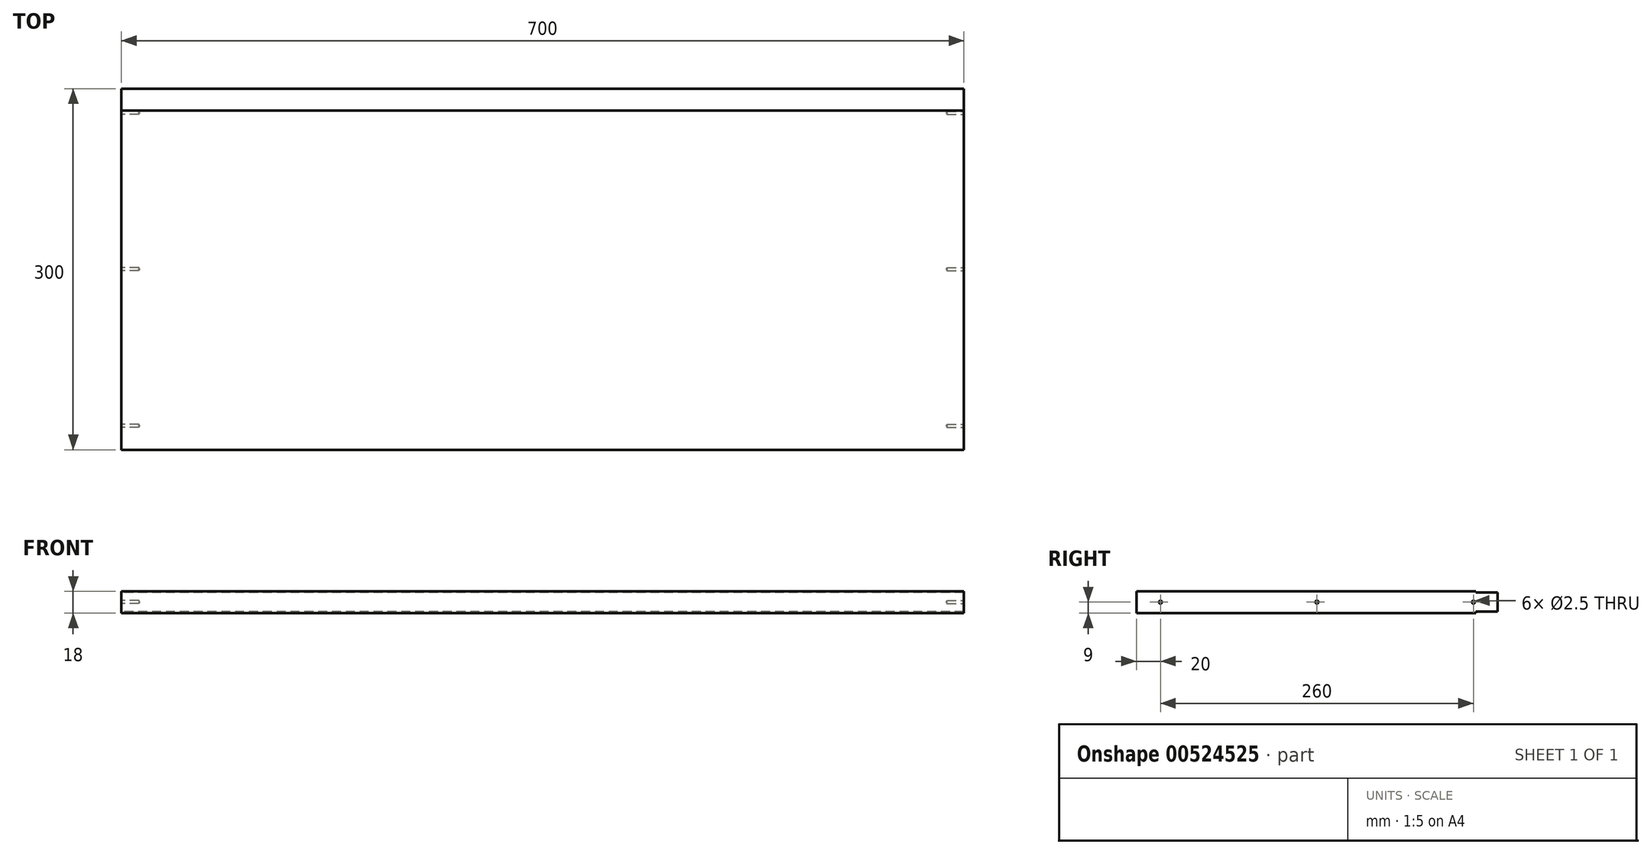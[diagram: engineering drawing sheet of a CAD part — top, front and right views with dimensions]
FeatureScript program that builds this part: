
annotation { "Feature Type Name" : "Feature", "Feature Type Description" : "" }
export const myFeature = defineFeature(function(context is Context, id is Id, definition is map)
    precondition{}
    {
        {
            var Q0;
            Q0=qCreatedBy(makeId("Top.planeOp"),FACE);
            var sketch = newSketch(context, id + "F0", { "sketchPlane" : qUnion([Q0])});
            skLineSegment(sketch, "E0.bottom", {"start": v(0, 0) * mm, "end": v(700, 0) * mm});
            skLineSegment(sketch, "E0.top", {"start": v(0, 300) * mm, "end": v(700, 300) * mm});
            skLineSegment(sketch, "E0.left", {"start": v(0, 0) * mm, "end": v(0, 300) * mm});
            skLineSegment(sketch, "E0.right", {"start": v(700, 0) * mm, "end": v(700, 300) * mm});
            skSolve(sketch);
        }
        {
            var Q0;
            Q0 = qSketchRegion(id + "F0", true);
            extrude(context, id + "F1", {"entities" : qUnion([Q0]), "depth" : 18 * mm, "offsetDistance" : 25 * mm});
        }
        {
            var Q0;
            Q0=makeQuery(id+"F1.opExtrude","SWEPT_FACE",FACE,{"disambiguationData":[OSD([sQuery(id+"F0.wireOp",EDGE,"E0.left")])]});
            var sketch = newSketch(context, id + "F2", { "sketchPlane" : qUnion([Q0])});
            skLineSegment(sketch, "E1.bottom", {"start": v(-300, 18) * mm, "end": v(-282, 18) * mm});
            skLineSegment(sketch, "E1.top", {"start": v(-300, 17) * mm, "end": v(-282, 17) * mm});
            skLineSegment(sketch, "E1.left", {"start": v(-300, 18) * mm, "end": v(-300, 17) * mm});
            skLineSegment(sketch, "E1.right", {"start": v(-282, 18) * mm, "end": v(-282, 17) * mm});
            skLineSegment(sketch, "E2.bottom", {"start": v(-300, 0) * mm, "end": v(-282, 0) * mm});
            skLineSegment(sketch, "E2.top", {"start": v(-300, 1) * mm, "end": v(-282, 1) * mm});
            skLineSegment(sketch, "E2.left", {"start": v(-300, 0) * mm, "end": v(-300, 1) * mm});
            skLineSegment(sketch, "E2.right", {"start": v(-282, 0) * mm, "end": v(-282, 1) * mm});
            skSolve(sketch);
        }
        {
            var Q0;
            Q0 = qSketchRegion(id + "F2", true);
            extrude(context, id + "F3", {"entities" : qUnion([Q0]), "operationType" : NewBodyOperationType.REMOVE, "endBound" : BoundingType.THROUGH_ALL, "oppositeDirection" : true, "depth" : 25 * mm, "offsetDistance" : 25 * mm});
        }
        {
            var Q0;
            Q0=makeQuery(id+"F1.opExtrude","SWEPT_FACE",FACE,{"disambiguationData":[OSD([sQuery(id+"F0.wireOp",EDGE,"E0.left")])]});
            var sketch = newSketch(context, id + "F4", { "sketchPlane" : qUnion([Q0])});
            skPoint(sketch, "E3", {"position": v(-280, 9) * mm});
            skPoint(sketch, "E4", {"position": v(-150, 9) * mm});
            skPoint(sketch, "E5", {"position": v(-20, 9) * mm});
            skSolve(sketch);
        }
        {
            var Q0;
            Q0=sQuery(id+"F4.wireOp",VERTEX,"E3");
            var Q1;
            Q1=sQuery(id+"F4.wireOp",VERTEX,"E4");
            var Q2;
            Q2=sQuery(id+"F4.wireOp",VERTEX,"E5");
            var Q3;
            Q3=makeQuery(id+"F1.opExtrude","SWEPT_BODY",BODY,{"disambiguationData":[OSD([sQuery(id+"F0.wireOp",EDGE,"E0.bottom"),sQuery(id+"F0.wireOp",EDGE,"E0.top"),sQuery(id+"F0.wireOp",EDGE,"E0.left"),sQuery(id+"F0.wireOp",EDGE,"E0.right")])]});
            hole(context, id + "F5", {"style" : HoleStyle.SIMPLE, "endStyle" : HoleEndStyle.BLIND, "standardTappedOrClearance" : lookupTablePath({ "standard" : "ISO", "engagement" : "75%", "pitch" : "0.5 mm", "size" : "M3", "type" : "Tapped" }), "standardBlindInLast" : lookupTablePath({ "standard" : "ISO", "engagement" : "75%", "pitch" : "0.5 mm", "size" : "M3", "type" : "Tapped" }), "holeDiameter" : 2.5 * mm, "showTappedDepth" : true, "holeDepth" : 14.5 * mm, "isTappedThrough" : true, "tappedDepth" : 13 * mm, "tapClearance" : 3, "locations" : qUnion([Q0, Q1, Q2]), "scope" : qUnion([Q3]), "majorDiameter" : 3 * mm});
        }
        {
            var Q0;
            Q0=makeQuery(id+"F1.opExtrude","SWEPT_FACE",FACE,{"disambiguationData":[OSD([sQuery(id+"F0.wireOp",EDGE,"E0.right")])]});
            var sketch = newSketch(context, id + "F6", { "sketchPlane" : qUnion([Q0])});
            skPoint(sketch, "E6", {"position": v(20, 9) * mm});
            skPoint(sketch, "E7", {"position": v(150, 9) * mm});
            skPoint(sketch, "E8", {"position": v(360.42, 9) * mm});
            skPoint(sketch, "E9", {"position": v(280, 9) * mm});
            skSolve(sketch);
        }
        {
            var Q0;
            Q0=sQuery(id+"F6.wireOp",VERTEX,"E6");
            var Q1;
            Q1=sQuery(id+"F6.wireOp",VERTEX,"E7");
            var Q2;
            Q2=sQuery(id+"F6.wireOp",VERTEX,"E9");
            var Q3;
            Q3=makeQuery(id+"F1.opExtrude","SWEPT_BODY",BODY,{"disambiguationData":[OSD([sQuery(id+"F0.wireOp",EDGE,"E0.bottom"),sQuery(id+"F0.wireOp",EDGE,"E0.top"),sQuery(id+"F0.wireOp",EDGE,"E0.left"),sQuery(id+"F0.wireOp",EDGE,"E0.right")])]});
            hole(context, id + "F7", {"style" : HoleStyle.SIMPLE, "endStyle" : HoleEndStyle.BLIND, "standardTappedOrClearance" : lookupTablePath({ "standard" : "ISO", "engagement" : "75%", "pitch" : "0.5 mm", "size" : "M3", "type" : "Tapped" }), "standardBlindInLast" : lookupTablePath({ "standard" : "ISO", "engagement" : "75%", "pitch" : "0.5 mm", "size" : "M3", "type" : "Tapped" }), "holeDiameter" : 2.5 * mm, "showTappedDepth" : true, "holeDepth" : 14 * mm, "isTappedThrough" : true, "tappedDepth" : 12.5 * mm, "tapClearance" : 3, "locations" : qUnion([Q0, Q1, Q2]), "scope" : qUnion([Q3]), "majorDiameter" : 3 * mm});
        }
    });
